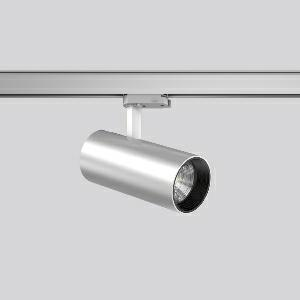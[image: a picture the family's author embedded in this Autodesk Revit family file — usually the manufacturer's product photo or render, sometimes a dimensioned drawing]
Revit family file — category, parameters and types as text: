
# Revit family: deecos_s_mini_742200_004_2_3305
name_source: partatom
category: Lighting Fixtures
units: mm (PartAtom-declared; Revit-internal decimal feet)

## family parameters
Cut with Voids When Loaded = No
Host = Face
Light Source = No
Part Type = Normal
Room Calculation Point = No
Round Connector Dimension = Use Diameter
Shared = No

## types (1)
- DEECOS S mini (1 x LED Modul 927, 1900 lm, 2700)
    Apparent Load = 20 VA
    Approval mark = CE
    CIE Flux Codes = 98 100 100 100 100
    Color Rendering = 92
    Color Temperature = 2700
    Default Elevation = 1800 mm
    Description = Series: DEECOS S mini
LED surface-mounted projector in modern design with no visible cooling ribs. Housing: die-cast aluminium, powder-coated. Rotation range: 356°. Swivel range: 90°. Black plastic ring and recessed LED to prevent glare from the side. Optical assembly with lens made of plastic (polycarbonate) for the best homogeneous light distribution - can be changed without tools. Best colour rendering index Ra>90. With multi adaptor for 3-circuit tracks 230 V. Suitable for Track on ceiling, Wall track. High quality converter without flickering and stroboscopic effect. The following accessories can be mounted without use of tools: interchangeable lenses, decorative glasses, honeycomb louvre, clear and frosted diffusers, white interchangeable plastic ring. 
Colour: silver
Diameter: 87 mm
Height: 214 mm
Lamp: LED
Socket: without socket
Colour temperature: 2700K
Colour rendering index (CRI): 92
System power: 20 W
Rated luminous flux: 1900 lm
Luminous efficiency: 95 lm/W
Control gear: Regulated power supply
Protection class: I
Type of protection: IP 20
    Height = 214 mm
    Lamp = 1 x LED Modul 927
    Lamp Light Flux = 1900 lm
    Lamp count = 1
    Length = 87 mm
    Lifetime = 50000 h
    Luminous efficacy = 95 lm/W
    Manufacturer = RZB
    ModVariant = No
    Model = 742200.004.2
    Mounting Place = Ceiling
    Mounting Type = Rail mounted
    Number of Poles = 1
    OnlyDefault = Yes
    Power Factor = 1
    Product Name = DEECOS S mini
    Product group = Track mounted projectors
    ProductGroupID = 301
    Protection Class = Protection class I
    Protection Degree = IP 20
    RLX_Detail_Level = 1
    RLX_Emergency_Light_Flux = 0 lm
    RLX_Emergency_Type = 0
    RLX_Emergency_Type_DB = No
    RlxData = <blob elided: 37469 chars, md5=ddbcd365>
    Socket = socket
    Standby Power = 0 W
    System Light Flux = 1900 lm
    System Power = 20 W
    Type Comments = Product without accessories
    Type Image = 741930.004.jpg
    URL = http://relux.com
    VarID = ---
    Voltage = 230 V
    Voltage Range = 220-240 V
    Weight = 0.00 kg
    Width = 0 mm  [stored 0 ft]

note: [stored X ft] marks values corroborated as IEEE doubles in the binary element streams (Revit-internal decimal feet)

## geometry (parser evidence)
native form markers: Blend x4, Sweep x11
no freeform markers — native parametric forms only
